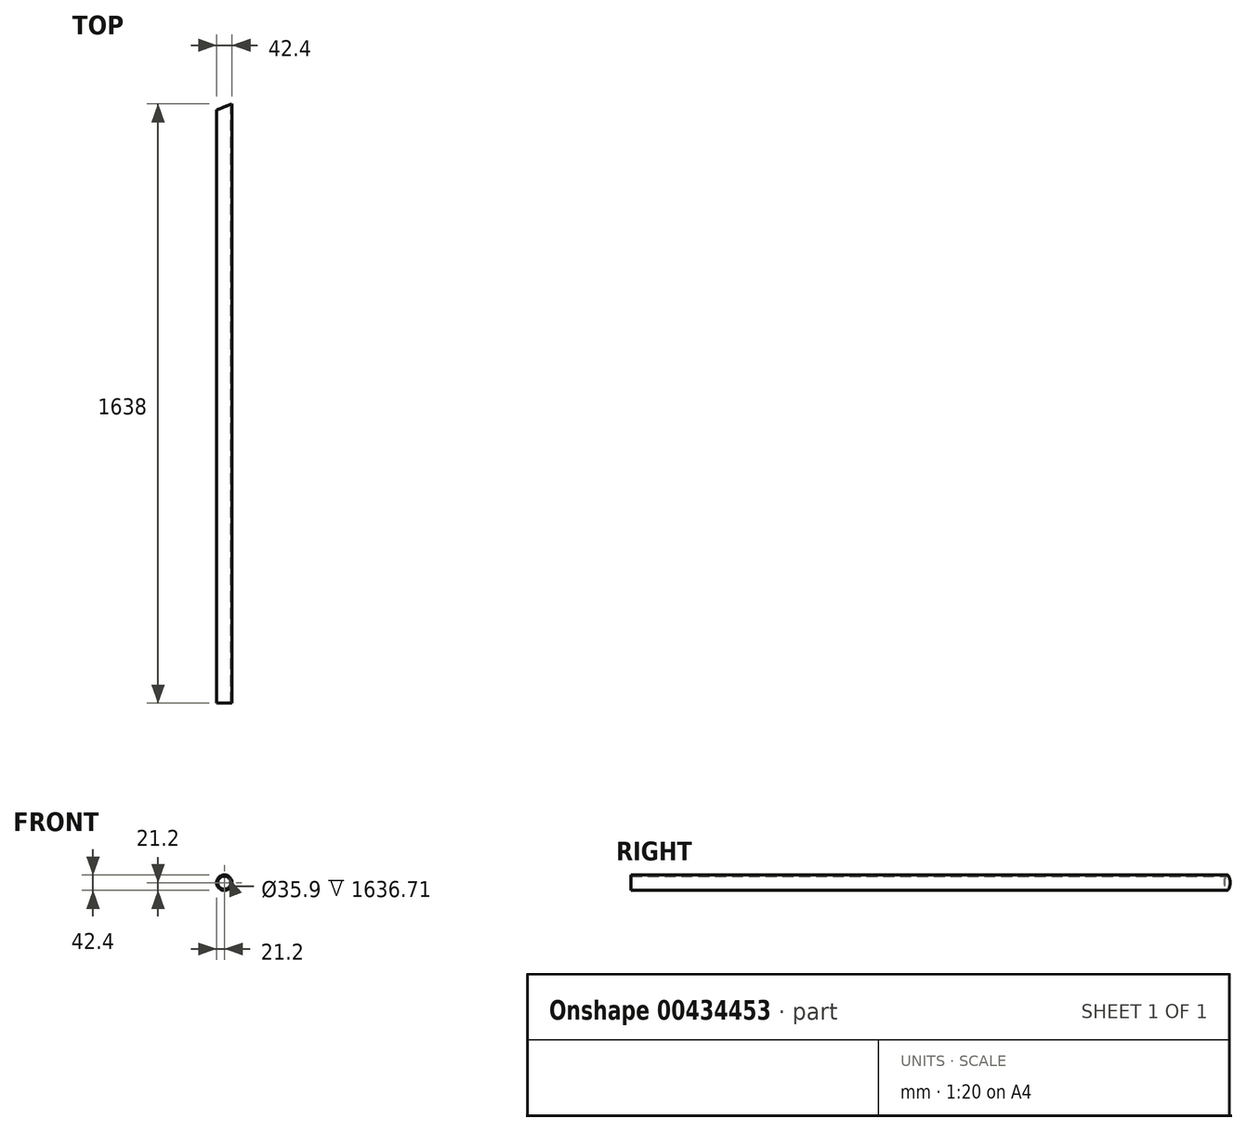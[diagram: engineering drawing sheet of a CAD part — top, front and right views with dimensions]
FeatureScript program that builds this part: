
annotation { "Feature Type Name" : "Feature", "Feature Type Description" : "" }
export const myFeature = defineFeature(function(context is Context, id is Id, definition is map)
    precondition{}
    {
        {
            var Q0;
            Q0=qCreatedBy(makeId("Front.planeOp"),FACE);
            var sketch = newSketch(context, id + "F0", { "sketchPlane" : qUnion([Q0])});
            skCircle(sketch, "E0", {"center": v(0, 0) * mm, "radius": 21.2 * mm});
            skCircle(sketch, "E1", {"center": v(0, 0) * mm, "radius": 17.95 * mm});
            skSolve(sketch);
        }
        {
            var Q0;
            Q0 = qSketchRegion(id + "F0", true);
            extrude(context, id + "F1", {"entities" : qUnion([Q0]), "depth" : 1638 * mm, "offsetDistance" : 25 * mm});
        }
        {
            var Q0;
            Q0=qCreatedBy(makeId("Top.planeOp"),FACE);
            var sketch = newSketch(context, id + "F2", { "sketchPlane" : qUnion([Q0])});
            skLineSegment(sketch, "E2", {"start": v(-21.2, -16.88) * mm, "end": v(21.2, 0) * mm});
            skLineSegment(sketch, "E3", {"start": v(21.2, 0) * mm, "end": v(-21.2, 0) * mm});
            skLineSegment(sketch, "E4", {"start": v(-21.2, 0) * mm, "end": v(-21.2, -16.88) * mm});
            skSolve(sketch);
        }
        {
            var Q0;
            Q0 = qSketchRegion(id + "F2", true);
            extrude(context, id + "F3", {"entities" : qUnion([Q0]), "operationType" : NewBodyOperationType.REMOVE, "endBound" : BoundingType.THROUGH_ALL, "oppositeDirection" : true, "depth" : 25 * mm, "offsetDistance" : 25 * mm, "hasSecondDirection" : true, "secondDirectionBound" : SecondDirectionBoundingType.THROUGH_ALL, "secondDirectionOppositeDirection" : false, "secondDirectionDepth" : 25 * mm});
        }
    });
